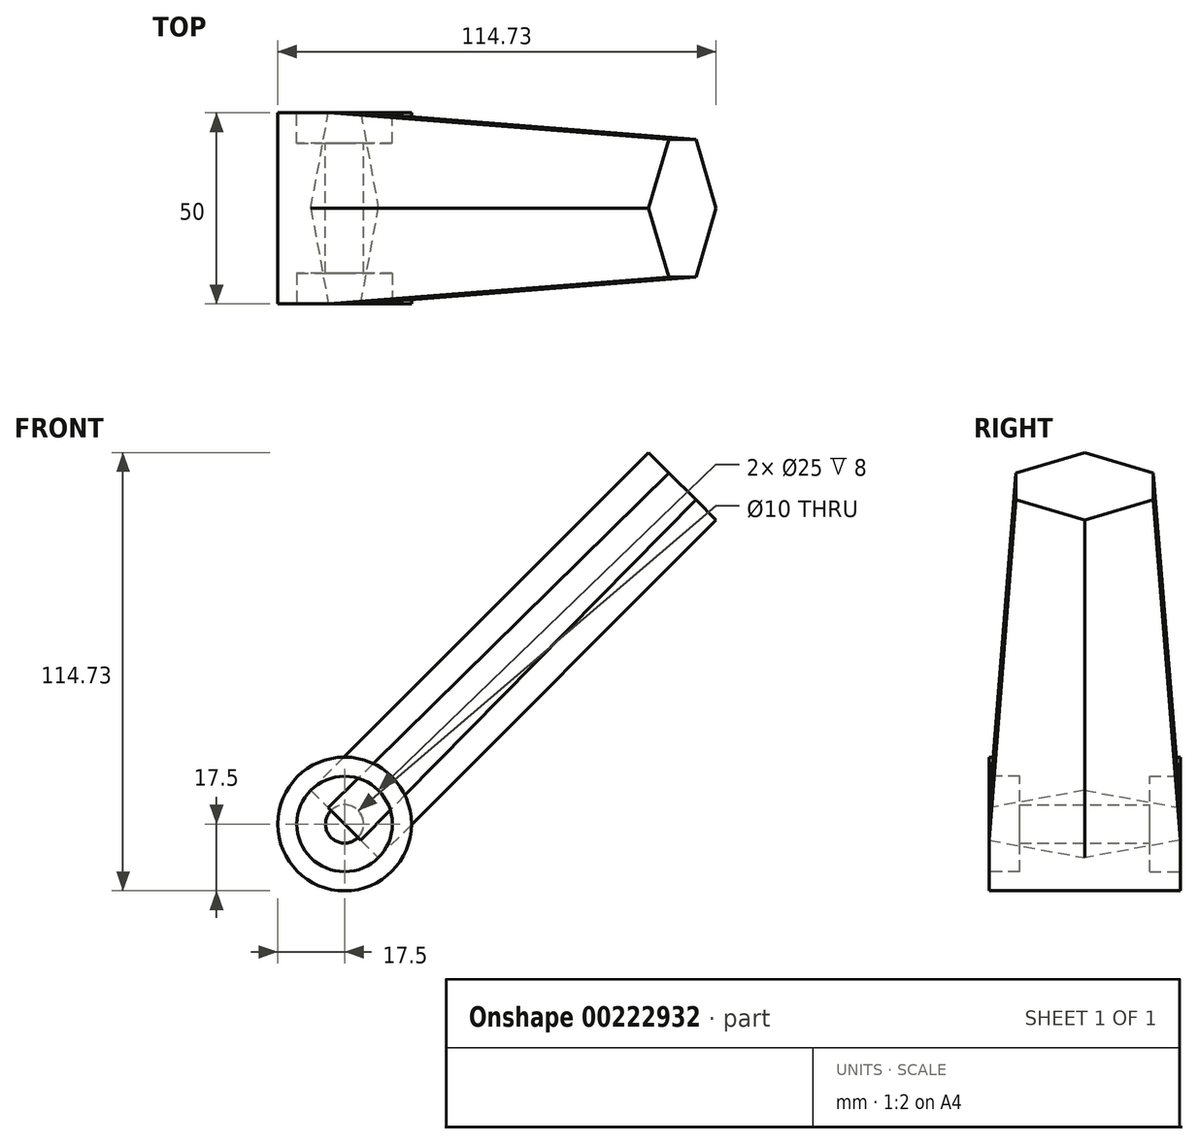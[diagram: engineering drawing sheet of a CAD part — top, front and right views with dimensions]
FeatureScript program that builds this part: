
annotation { "Feature Type Name" : "Feature", "Feature Type Description" : "" }
export const myFeature = defineFeature(function(context is Context, id is Id, definition is map)
    precondition{}
    {
        {
            var Q0;
            Q0=qCreatedBy(makeId("Front.planeOp"),FACE);
            var sketch = newSketch(context, id + "F0", { "sketchPlane" : qUnion([Q0])});
            skCircle(sketch, "E0", {"center": v(0, 0) * mm, "radius": 125 * mm});
            skLineSegment(sketch, "E1", {"start": v(0, 0) * mm, "end": v(0, 125) * mm});
            skLineSegment(sketch, "E2", {"start": v(0, 0) * mm, "end": v(125, 0) * mm});
            skLineSegment(sketch, "E3", {"start": v(0, 0) * mm, "end": v(88.39, 88.39) * mm});
            skLineSegment(sketch, "E4", {"start": v(0, 125) * mm, "end": v(125, 0) * mm});
            skPoint(sketch, "E5", {"position": v(62.5, 62.5) * mm});
            skCircle(sketch, "E6", {"center": v(0, 0) * mm, "radius": 12.5 * mm});
            skSolve(sketch);
        }
        {
            var Q0;
            Q0=qCreatedBy(makeId("Front.planeOp"),FACE);
            var sketch = newSketch(context, id + "F1", { "sketchPlane" : qUnion([Q0])});
            skCircle(sketch, "E7", {"center": v(0, 0) * mm, "radius": 17.5 * mm});
            skLineSegment(sketch, "E8", {"start": v(17.5, 0) * mm, "end": v(12.5, 0) * mm, "construction": true});
            skCircle(sketch, "E9", {"center": v(0, 0) * mm, "radius": 5 * mm});
            skSolve(sketch);
        }
        {
            var Q0;
            Q0=makeQuery(id+"F1.imprint","IMPRINT",FACE,{"disambiguationData":[TD([[makeQuery(id+"F1.imprint","IMPRINT",EDGE,{"derivedFrom":sQuery(id+"F1.wireOp",EDGE,"E7")}),1.0]])]});
            extrude(context, id + "F2", {"entities" : qUnion([Q0]), "depth" : 25 * mm});
        }
        {
            var Q0;
            Q0=makeQuery(id+"F2.opExtrude","CAP_FACE",FACE,{"disambiguationData":[OSD([sQuery(id+"F1.wireOp",EDGE,"E7"),sQuery(id+"F1.wireOp",EDGE,"E9")])],"isStart":false});
            var sketch = newSketch(context, id + "F3", { "sketchPlane" : qUnion([Q0])});
            skCircle(sketch, "E10.0", {"center": v(0, 0) * mm, "radius": 12.5 * mm});
            skSolve(sketch);
        }
        {
            var Q0;
            Q0 = qSketchRegion(id + "F3", true);
            extrude(context, id + "F4", {"entities" : qUnion([Q0]), "operationType" : NewBodyOperationType.REMOVE, "oppositeDirection" : true, "depth" : 8 * mm});
        }
        {
            var Q0;
            Q0=makeQuery(id+"F2.opExtrude","SWEPT_BODY",BODY,{"disambiguationData":[OSD([sQuery(id+"F1.wireOp",EDGE,"E7"),sQuery(id+"F1.wireOp",EDGE,"E9")])]});
            var Q1;
            Q1=qCreatedBy(makeId("Front.planeOp"),FACE);
            mirror(context, id + "F5", {"operationType" : NewBodyOperationType.ADD, "entities" : qUnion([Q0]), "mirrorPlane" : qUnion([Q1])});
        }
        {
            var Q0;
            Q0=sQuery(id+"F0.wireOp",EDGE,"E3");
            var Q1;
            Q1=sQuery(id+"F0.wireOp",VERTEX,"E3.end");
            cPlane(context, id + "F6", {"entities" : qUnion([Q0, Q1]), "cplaneType" : CPlaneType.CURVE_POINT, "offset" : 25 * mm, "width" : 150 * mm, "height" : 150 * mm});
        }
        {
            var Q0;
            Q0=qCreatedBy(id+"F6.planeOp",FACE);
            var sketch = newSketch(context, id + "F7", { "sketchPlane" : qUnion([Q0])});
            skLineSegment(sketch, "E11.0", {"start": v(0, 88.39) * mm, "end": v(0, -88.39) * mm, "construction": true});
            skLineSegment(sketch, "E12", {"start": v(0, 12.5) * mm, "end": v(-18, 5) * mm});
            skLineSegment(sketch, "E13", {"start": v(-18, 5) * mm, "end": v(-18, -5) * mm});
            skLineSegment(sketch, "E14", {"start": v(-18, -5) * mm, "end": v(0, -12.5) * mm});
            skLineSegment(sketch, "E15", {"start": v(0, 0) * mm, "end": v(-33.38, 0) * mm, "construction": true});
            skLineSegment(sketch, "E16.MirrorCS", {"start": v(0, 12.5) * mm, "end": v(18, 5) * mm});
            skLineSegment(sketch, "E17.MirrorCS", {"start": v(0, 0) * mm, "end": v(33.38, 0) * mm, "construction": true});
            skLineSegment(sketch, "E18.MirrorCS", {"start": v(18, 5) * mm, "end": v(18, -5) * mm});
            skLineSegment(sketch, "E19.MirrorCS", {"start": v(18, -5) * mm, "end": v(0, -12.5) * mm});
            skSolve(sketch);
        }
        {
            var Q0;
            Q0=sQuery(id+"F0.wireOp",EDGE,"E3");
            var Q1;
            Q1=sQuery(id+"F0.wireOp",VERTEX,"E6.center");
            cPlane(context, id + "F8", {"entities" : qUnion([Q0, Q1]), "cplaneType" : CPlaneType.CURVE_POINT, "offset" : 25 * mm, "width" : 150 * mm, "height" : 150 * mm});
        }
        {
            var Q0;
            Q0=qCreatedBy(id+"F8.planeOp",FACE);
            var sketch = newSketch(context, id + "F9", { "sketchPlane" : qUnion([Q0])});
            skLineSegment(sketch, "E20.0", {"start": v(18, -5) * mm, "end": v(0, -12.5) * mm, "construction": true});
            skLineSegment(sketch, "E21.0", {"start": v(18, 5) * mm, "end": v(18, -5) * mm, "construction": true});
            skLineSegment(sketch, "E22.0", {"start": v(0, 12.5) * mm, "end": v(18, 5) * mm, "construction": true});
            skLineSegment(sketch, "E23.0", {"start": v(0, 12.5) * mm, "end": v(-18, 5) * mm, "construction": true});
            skLineSegment(sketch, "E24.0", {"start": v(-18, 5) * mm, "end": v(-18, -5) * mm, "construction": true});
            skLineSegment(sketch, "E25.0", {"start": v(-18, -5) * mm, "end": v(0, -12.5) * mm, "construction": true});
            skLineSegment(sketch, "E26", {"start": v(-25, 6) * mm, "end": v(-25, -6) * mm});
            skLineSegment(sketch, "E27", {"start": v(-25, -6) * mm, "end": v(0, -12.5) * mm});
            skLineSegment(sketch, "E28", {"start": v(-18, 0) * mm, "end": v(-50.72, 0) * mm, "construction": true});
            skLineSegment(sketch, "E29", {"start": v(0, 12.5) * mm, "end": v(-25, 6) * mm});
            skLineSegment(sketch, "E30", {"start": v(0, 12.5) * mm, "end": v(0, -12.5) * mm, "construction": true});
            skLineSegment(sketch, "E31.MirrorCS", {"start": v(25, -6) * mm, "end": v(0, -12.5) * mm});
            skLineSegment(sketch, "E32.MirrorCS", {"start": v(25, 6) * mm, "end": v(25, -6) * mm});
            skLineSegment(sketch, "E33.MirrorCS", {"start": v(0, 12.5) * mm, "end": v(25, 6) * mm});
            skSolve(sketch);
        }
        {
            var Q1;
            Q1 = qSketchRegion(id + "F7", true);
            var Q2;
            Q2 = qSketchRegion(id + "F9", true);
            loft(context, id + "F10", {"sheetProfilesArray" : [{ "sheetProfileEntities" : qUnion([Q1]) }, { "sheetProfileEntities" : qUnion([Q2]) }]});
        }
    });
